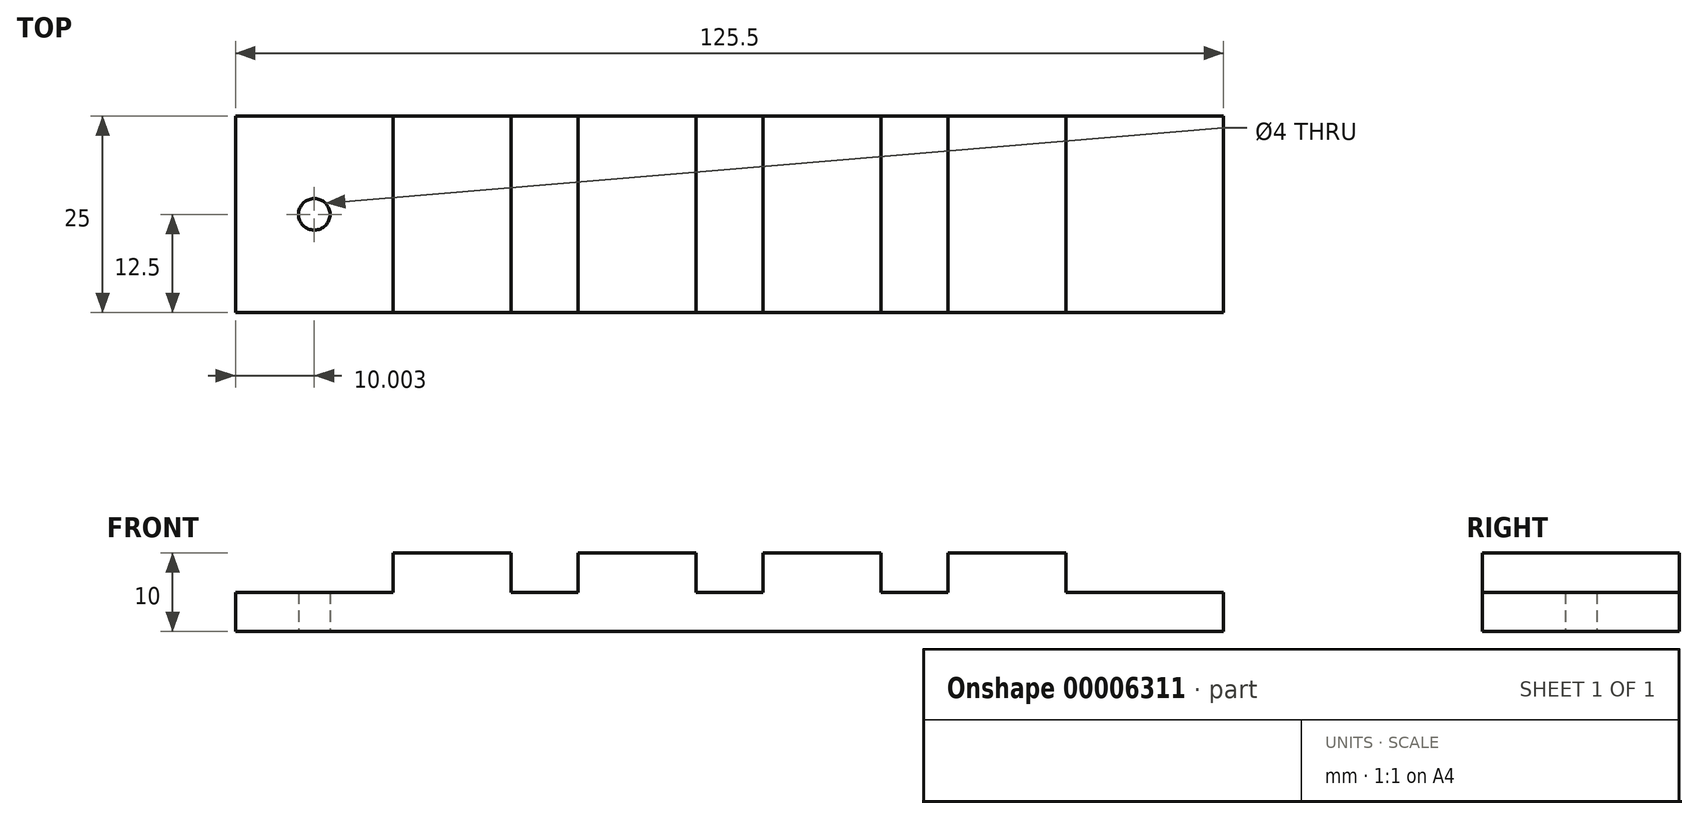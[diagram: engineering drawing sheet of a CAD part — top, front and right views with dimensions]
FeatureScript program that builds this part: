
annotation { "Feature Type Name" : "Feature", "Feature Type Description" : "" }
export const myFeature = defineFeature(function(context is Context, id is Id, definition is map)
    precondition{}
    {
        {
            var Q0;
            Q0=qCreatedBy(makeId("Front.planeOp"),FACE);
            var sketch = newSketch(context, id + "F0", { "sketchPlane" : qUnion([Q0])});
            skLineSegment(sketch, "E0", {"start": v(-191.29, 0) * mm, "end": v(-191.29, 5) * mm});
            skLineSegment(sketch, "E1", {"start": v(-171.29, 5) * mm, "end": v(-171.29, 10) * mm});
            skLineSegment(sketch, "E2", {"start": v(-171.29, 10) * mm, "end": v(-156.29, 10) * mm});
            skLineSegment(sketch, "E3", {"start": v(-156.29, 10) * mm, "end": v(-156.29, 5) * mm});
            skLineSegment(sketch, "E4", {"start": v(-156.29, 5) * mm, "end": v(-147.79, 5) * mm});
            skLineSegment(sketch, "E5", {"start": v(-147.79, 5) * mm, "end": v(-147.79, 10) * mm});
            skLineSegment(sketch, "E6", {"start": v(-147.79, 10) * mm, "end": v(-132.79, 10) * mm});
            skLineSegment(sketch, "E7", {"start": v(-132.79, 10) * mm, "end": v(-132.79, 5) * mm});
            skLineSegment(sketch, "E8", {"start": v(-132.79, 5) * mm, "end": v(-124.29, 5) * mm});
            skLineSegment(sketch, "E9", {"start": v(-124.29, 5) * mm, "end": v(-124.29, 10) * mm});
            skLineSegment(sketch, "E10", {"start": v(-124.29, 10) * mm, "end": v(-109.29, 10) * mm});
            skLineSegment(sketch, "E11", {"start": v(-109.29, 10) * mm, "end": v(-109.29, 5) * mm});
            skLineSegment(sketch, "E12", {"start": v(-109.29, 5) * mm, "end": v(-100.79, 5) * mm});
            skLineSegment(sketch, "E13", {"start": v(-100.79, 5) * mm, "end": v(-100.79, 10) * mm});
            skLineSegment(sketch, "E14", {"start": v(-100.79, 10) * mm, "end": v(-85.79, 10) * mm});
            skLineSegment(sketch, "E15", {"start": v(-85.79, 10) * mm, "end": v(-85.79, 5) * mm});
            skLineSegment(sketch, "E16", {"start": v(-65.79, 5) * mm, "end": v(-65.79, 0) * mm});
            skLineSegment(sketch, "E17", {"start": v(-65.79, 0) * mm, "end": v(-191.29, 0) * mm});
            skLineSegment(sketch, "E18.trimOffspring", {"start": v(-85.79, 5) * mm, "end": v(-65.79, 5) * mm});
            skLineSegment(sketch, "E19", {"start": v(-171.29, 5) * mm, "end": v(-191.29, 5) * mm});
            skLineSegment(sketch, "E20", {"start": v(-181.29, 5) * mm, "end": v(-181.29, -11.02) * mm, "construction": true});
            skSolve(sketch);
        }
        {
            var Q0;
            Q0=makeQuery(id+"F0.imprint","IMPRINT",FACE,{"disambiguationData":[TD([[makeQuery(id+"F0.imprint","IMPRINT",EDGE,{"derivedFrom":sQuery(id+"F0.wireOp",EDGE,"E0")}),-1.0]])]});
            extrude(context, id + "F1", {"entities" : qUnion([Q0]), "depth" : 25 * mm});
        }
        {
            var Q0;
            Q0=qCreatedBy(makeId("Top.planeOp"),FACE);
            var sketch = newSketch(context, id + "F2", { "sketchPlane" : qUnion([Q0])});
            skCircle(sketch, "E21", {"center": v(-181.29, -12.5) * mm, "radius": 2 * mm});
            skLineSegment(sketch, "E22", {"start": v(-191.29, -12.5) * mm, "end": v(-65.79, -12.5) * mm, "construction": true});
            skLineSegment(sketch, "E23", {"start": v(-128.54, 20.47) * mm, "end": v(-128.54, -12.5) * mm, "construction": true});
            skCircle(sketch, "E24.1.MirrorC", {"center": v(-75.79, -12.5) * mm, "radius": 2 * mm});
            skSolve(sketch);
        }
        {
            var Q0;
            Q0=makeQuery(id+"F2.imprint","IMPRINT",FACE,{"disambiguationData":[TD([[makeQuery(id+"F2.imprint","IMPRINT",EDGE,{"derivedFrom":sQuery(id+"F2.wireOp",EDGE,"E21")}),1.0]])]});
            var Q1;
            Q1=makeQuery(id+"F2.imprint","IMPRINT",FACE,{"disambiguationData":[TD([[makeQuery(id+"F2.imprint","IMPRINT",EDGE,{"derivedFrom":sQuery(id+"F2.wireOp",EDGE,"E24.1.MirrorC")}),-1.0]])]});
            var Q2;
            Q2=sQuery(id+"F2.wireOp",EDGE,"E21");
            extrude(context, id + "F3", {"entities" : qUnion([Q0, Q1]), "operationType" : NewBodyOperationType.REMOVE, "surfaceEntities" : qUnion([Q2]), "endBound" : BoundingType.THROUGH_ALL, "depth" : 25 * mm});
        }
    });
